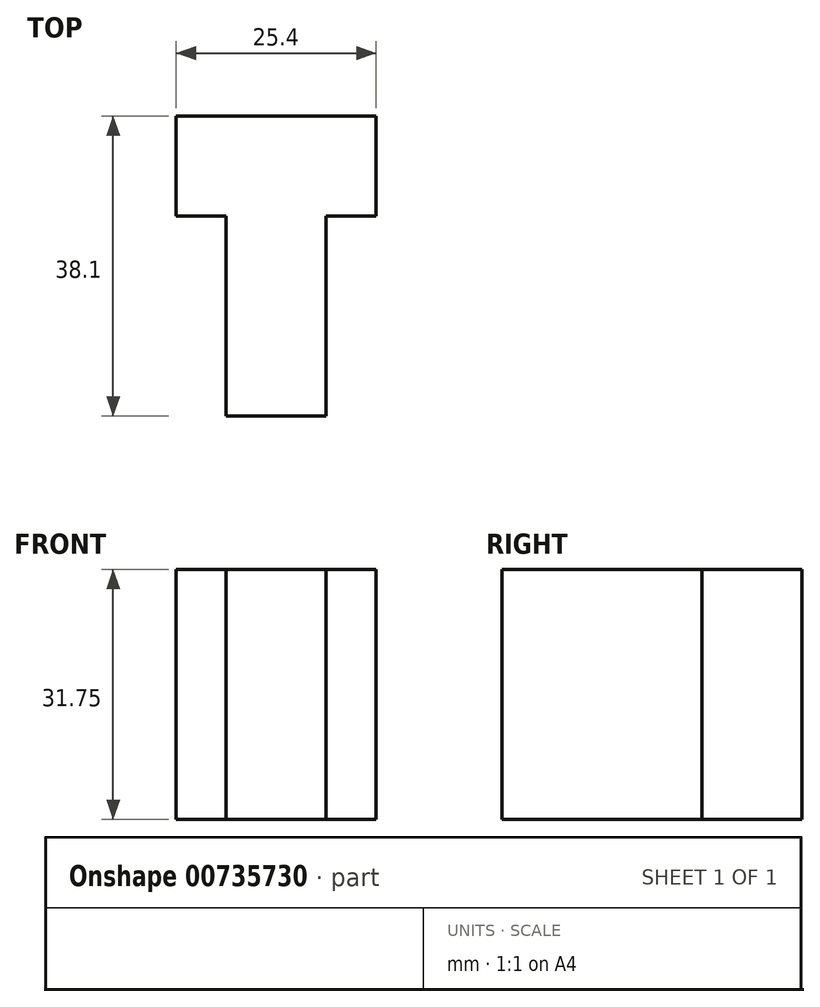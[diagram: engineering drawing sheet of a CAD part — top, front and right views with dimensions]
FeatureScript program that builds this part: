
annotation { "Feature Type Name" : "Feature", "Feature Type Description" : "" }
export const myFeature = defineFeature(function(context is Context, id is Id, definition is map)
    precondition{}
    {
        {
            var Q0;
            Q0=qCreatedBy(makeId("Top.planeOp"),FACE);
            var sketch = newSketch(context, id + "F0", { "sketchPlane" : qUnion([Q0])});
            skLineSegment(sketch, "E0", {"start": v(0, 0) * mm, "end": v(0, 25.4) * mm});
            skLineSegment(sketch, "E1", {"start": v(0, 25.4) * mm, "end": v(-6.35, 25.4) * mm});
            skLineSegment(sketch, "E2", {"start": v(-6.35, 25.4) * mm, "end": v(-6.35, 38.1) * mm});
            skLineSegment(sketch, "E3", {"start": v(-6.35, 38.1) * mm, "end": v(19.05, 38.1) * mm});
            skLineSegment(sketch, "E4", {"start": v(19.05, 38.1) * mm, "end": v(19.05, 25.4) * mm});
            skLineSegment(sketch, "E5", {"start": v(19.05, 25.4) * mm, "end": v(12.7, 25.4) * mm});
            skLineSegment(sketch, "E6", {"start": v(12.7, 25.4) * mm, "end": v(12.7, 0) * mm});
            skLineSegment(sketch, "E7", {"start": v(12.7, 0) * mm, "end": v(0, 0) * mm});
            skSolve(sketch);
        }
        {
            var Q0;
            Q0=makeQuery(id+"F0.imprint","IMPRINT",FACE,{"disambiguationData":[TD([[makeQuery(id+"F0.imprint","IMPRINT",EDGE,{"derivedFrom":sQuery(id+"F0.wireOp",EDGE,"E0")}),-1.0]])]});
            extrude(context, id + "F1", {"entities" : qUnion([Q0]), "depth" : 31.75 * mm, "offsetDistance" : 25.4 * mm});
        }
    });
